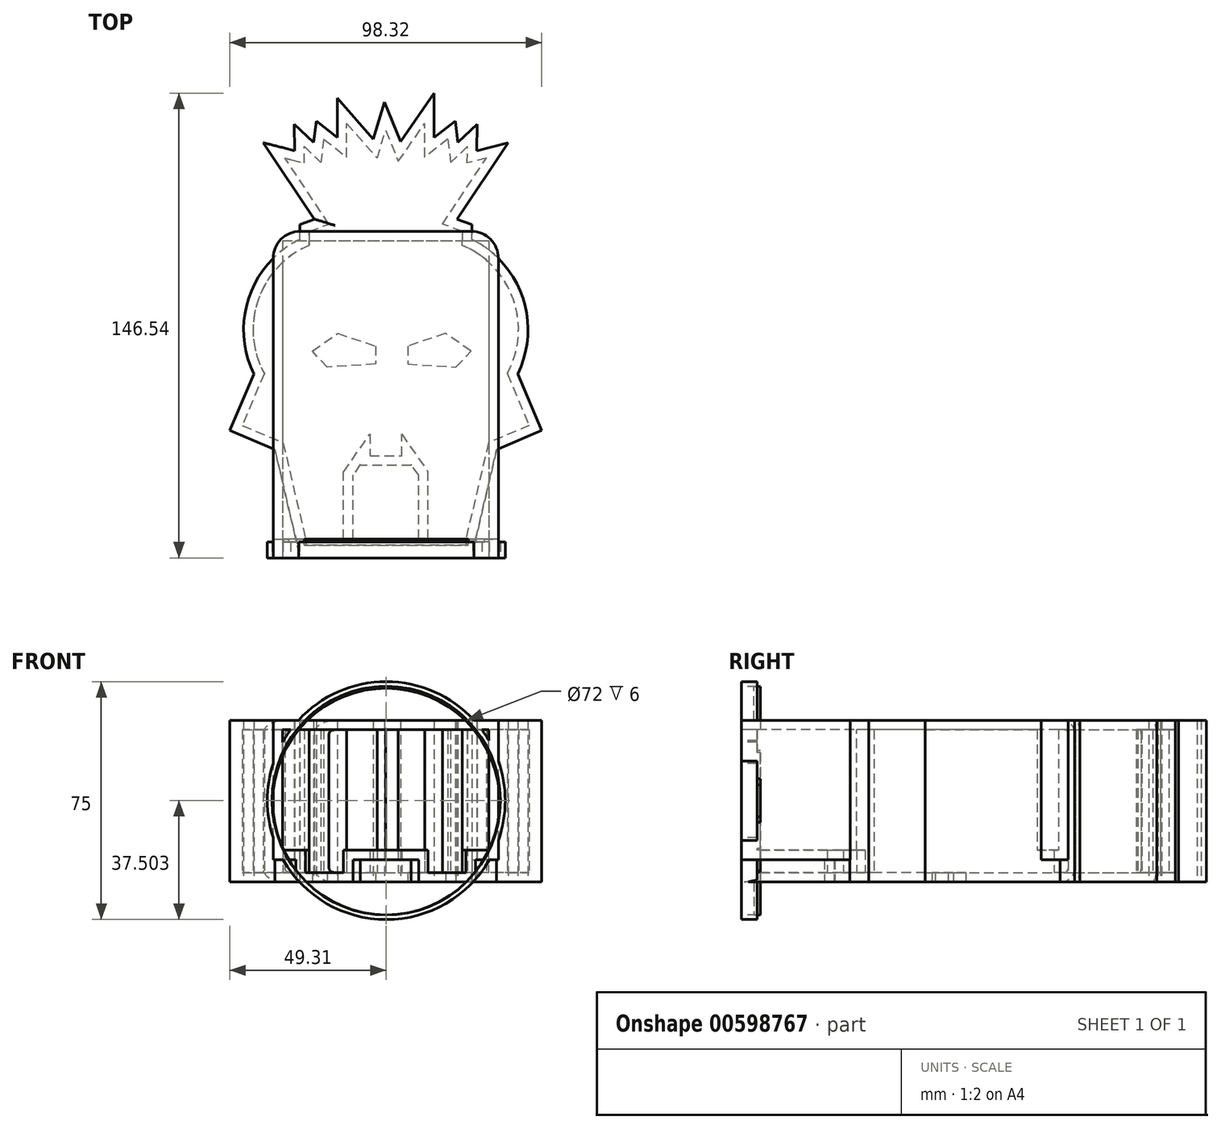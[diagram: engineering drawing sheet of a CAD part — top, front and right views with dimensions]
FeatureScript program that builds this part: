
annotation { "Feature Type Name" : "Feature", "Feature Type Description" : "" }
export const myFeature = defineFeature(function(context is Context, id is Id, definition is map)
    precondition{}
    {
        {
            var Q0;
            Q0=qCreatedBy(makeId("Top.planeOp"),FACE);
            var sketch = newSketch(context, id + "F0", { "sketchPlane" : qUnion([Q0])});
            skLineSegment(sketch, "E0", {"start": v(-38.3, -12.71) * mm, "end": v(-45.23, -29.07) * mm});
            skLineSegment(sketch, "E1", {"start": v(-45.23, -29.07) * mm, "end": v(-32.38, -34.51) * mm});
            skLineSegment(sketch, "E2", {"start": v(-32.38, -34.51) * mm, "end": v(-23.85, -70.83) * mm});
            skLineSegment(sketch, "E3", {"start": v(-23.85, -70.83) * mm, "end": v(-13.34, -70.83) * mm});
            skLineSegment(sketch, "E4", {"start": v(-13.34, -70.83) * mm, "end": v(-13.34, -43.75) * mm});
            skLineSegment(sketch, "E5", {"start": v(-13.34, -43.75) * mm, "end": v(-5, -31.79) * mm});
            skLineSegment(sketch, "E6", {"start": v(-5, -31.79) * mm, "end": v(-5, -38.64) * mm});
            skLineSegment(sketch, "E7", {"start": v(-5, -38.64) * mm, "end": v(0, -38.64) * mm});
            skLineSegment(sketch, "E8", {"start": v(-17.87, 34.44) * mm, "end": v(-31.74, 55.24) * mm});
            skLineSegment(sketch, "E9", {"start": v(-24.11, 32.15) * mm, "end": v(-17.87, 34.44) * mm});
            skLineSegment(sketch, "E10", {"start": v(-25.74, 58.87) * mm, "end": v(-20.48, 53.84) * mm});
            skLineSegment(sketch, "E11", {"start": v(-12.28, 55.5) * mm, "end": v(-12.28, 66.16) * mm});
            skLineSegment(sketch, "E12", {"start": v(-12.28, 66.16) * mm, "end": v(-2.75, 55.24) * mm});
            skLineSegment(sketch, "E13", {"start": v(-2.75, 55.24) * mm, "end": v(0, 64) * mm});
            skLineSegment(sketch, "E14", {"start": v(-19.56, 61.27) * mm, "end": v(-12.28, 55.5) * mm});
            skLineSegment(sketch, "E15", {"start": v(-19.56, 61.27) * mm, "end": v(-20.48, 53.84) * mm});
            skArc(sketch, "E16", {"start": v(-24.11, 27.73) * mm, "mid": v(-40.2, 10.66) * mm, "end": v(-38.3, -12.71) * mm});
            skLineSegment(sketch, "E17", {"start": v(-31.74, 55.24) * mm, "end": v(-25.67, 53.67) * mm});
            skLineSegment(sketch, "E18", {"start": v(-25.67, 53.67) * mm, "end": v(-25.74, 58.87) * mm});
            skLineSegment(sketch, "E19", {"start": v(0, 79.09) * mm, "end": v(0, -69.65) * mm, "construction": true});
            skLineSegment(sketch, "E20.MirrorCS", {"start": v(25.67, 53.67) * mm, "end": v(25.74, 58.87) * mm});
            skLineSegment(sketch, "E21.MirrorCS", {"start": v(19.56, 61.27) * mm, "end": v(20.48, 53.84) * mm});
            skLineSegment(sketch, "E22.MirrorCS", {"start": v(19.56, 61.27) * mm, "end": v(12.28, 55.5) * mm});
            skLineSegment(sketch, "E23.MirrorCS", {"start": v(12.28, 55.5) * mm, "end": v(12.28, 66.16) * mm});
            skLineSegment(sketch, "E24.MirrorCS", {"start": v(25.74, 58.87) * mm, "end": v(20.48, 53.84) * mm});
            skLineSegment(sketch, "E25.MirrorCS", {"start": v(31.74, 55.24) * mm, "end": v(25.67, 53.67) * mm});
            skLineSegment(sketch, "E26.MirrorCS", {"start": v(24.11, 32.15) * mm, "end": v(17.87, 34.44) * mm});
            skLineSegment(sketch, "E27.MirrorCS", {"start": v(23.85, -70.83) * mm, "end": v(13.34, -70.83) * mm});
            skLineSegment(sketch, "E28.MirrorCS", {"start": v(32.38, -34.51) * mm, "end": v(23.85, -70.83) * mm});
            skLineSegment(sketch, "E29.MirrorCS", {"start": v(17.87, 34.44) * mm, "end": v(31.74, 55.24) * mm});
            skLineSegment(sketch, "E30.MirrorCS", {"start": v(13.34, -70.83) * mm, "end": v(13.34, -43.75) * mm});
            skLineSegment(sketch, "E31.MirrorCS", {"start": v(45.23, -29.07) * mm, "end": v(32.38, -34.51) * mm});
            skLineSegment(sketch, "E32.MirrorCS", {"start": v(38.3, -12.71) * mm, "end": v(45.23, -29.07) * mm});
            skArc(sketch, "E33.MirrorCS", {"start": v(24.11, 27.73) * mm, "mid": v(40.2, 10.66) * mm, "end": v(38.3, -12.71) * mm});
            skLineSegment(sketch, "E34", {"start": v(0, 64) * mm, "end": v(3.95, 54.2) * mm});
            skLineSegment(sketch, "E35", {"start": v(3.95, 54.2) * mm, "end": v(12.28, 66.16) * mm});
            skLineSegment(sketch, "E36", {"start": v(0, -38.64) * mm, "end": v(5, -38.64) * mm});
            skLineSegment(sketch, "E37", {"start": v(5, -38.64) * mm, "end": v(5, -31.79) * mm});
            skLineSegment(sketch, "E38", {"start": v(5, -31.79) * mm, "end": v(13.34, -43.75) * mm});
            skLineSegment(sketch, "E39", {"start": v(-24.11, 32.15) * mm, "end": v(-24.11, 27.73) * mm});
            skLineSegment(sketch, "E40", {"start": v(24.11, 32.15) * mm, "end": v(24.11, 27.73) * mm});
            skSolve(sketch);
        }
        {
            var Q0;
            Q0=qSketchRegion(id+"F0",true);
            extrude(context, id + "F1", {"entities" : qUnion([Q0]), "depth" : 45 * mm, "offsetDistance" : 25 * mm});
        }
        {
            var Q0;
            Q0=qCreatedBy(makeId("Top.planeOp"),FACE);
            var sketch = newSketch(context, id + "F2", { "sketchPlane" : qUnion([Q0])});
            skLineSegment(sketch, "E41", {"start": v(-23.16, -5.6) * mm, "end": v(-18.41, -10.67) * mm});
            skLineSegment(sketch, "E42", {"start": v(-18.41, -10.67) * mm, "end": v(-3.2, -9.69) * mm});
            skLineSegment(sketch, "E43", {"start": v(-3.2, -9.69) * mm, "end": v(-3.2, -4.02) * mm});
            skLineSegment(sketch, "E44", {"start": v(-3.2, -4.02) * mm, "end": v(-15.14, 0) * mm});
            skLineSegment(sketch, "E45", {"start": v(-15.14, 0) * mm, "end": v(-23.16, -5.6) * mm});
            skLineSegment(sketch, "E46", {"start": v(-15.14, 0) * mm, "end": v(-10.75, -1.03) * mm});
            skFitSpline(sketch, "E47", {"points": [v(-10.75, -1.03) * mm, v(-10.75, 2.44) * mm, v(-12.29, 3.2) * mm, v(-11.11, 6.02) * mm], "startDerivative": vector(-4.83, 8.14) * mm, "endDerivative": vector(5.33, 8.63) * mm});
            skLineSegment(sketch, "E48", {"start": v(1.86, -15.53) * mm, "end": v(1.86, 7.72) * mm, "construction": true});
            skLineSegment(sketch, "E49.MirrorCS", {"start": v(6.93, -9.69) * mm, "end": v(6.93, -4.02) * mm});
            skLineSegment(sketch, "E50.MirrorCS", {"start": v(22.13, -10.67) * mm, "end": v(6.93, -9.69) * mm});
            skLineSegment(sketch, "E51.MirrorCS", {"start": v(6.93, -4.02) * mm, "end": v(18.86, 0) * mm});
            skLineSegment(sketch, "E52.MirrorCS", {"start": v(26.88, -5.6) * mm, "end": v(22.13, -10.67) * mm});
            skLineSegment(sketch, "E53.MirrorCS", {"start": v(18.86, 0) * mm, "end": v(26.88, -5.6) * mm});
            skLineSegment(sketch, "E54.MirrorCS", {"start": v(18.86, 0) * mm, "end": v(14.47, -1.03) * mm});
            skFitSpline(sketch, "E55.MirrorCS", {"points": [v(14.47, -1.03) * mm, v(14.47, 2.44) * mm, v(16, 3.2) * mm, v(14.84, 6.02) * mm], "startDerivative": vector(4.83, 8.14) * mm, "endDerivative": vector(-5.33, 8.63) * mm});
            skPoint(sketch, "E56", {"position": v(1.86, 13.91) * mm});
            skSolve(sketch);
        }
        {
            var Q0;
            Q0=makeQuery(id+"F1.opExtrude","CAP_EDGE",EDGE,{"disambiguationData":[OSD([sQuery(id+"F0.wireOp",EDGE,"QlBGKe7W-CjFm-zpKe-syDU-rIZYVbdessFk")])],"isStart":false});
            var Q1;
            Q1=makeQuery(id+"F1.opExtrude","CAP_EDGE",EDGE,{"disambiguationData":[OSD([sQuery(id+"F0.wireOp",EDGE,"E210.MirrorCS")])],"isStart":false});
            var Q2;
            Q2=makeQuery(id+"F1.opExtrude","CAP_EDGE",EDGE,{"disambiguationData":[OSD([sQuery(id+"F0.wireOp",EDGE,"E9")])],"isStart":false});
            var Q3;
            Q3=makeQuery(id+"F1.opExtrude","CAP_EDGE",EDGE,{"disambiguationData":[OSD([sQuery(id+"F0.wireOp",EDGE,"E26.MirrorCS")])],"isStart":false});
            fillet(context, id + "F3", {"entities" : qUnion([Q0, Q1, Q2, Q3]), "radius" : 1.02 * mm, "tangentPropagation" : true, "allowEdgeOverflow" : false});
        }
        {
            var Q0;
            Q0=makeQuery(id+"F3.opFillet","BLEND_EDGE",EDGE,{"blendedFrom":[makeQuery(id+"F1.opExtrude","CAP_EDGE",EDGE,{"disambiguationData":[OSD([sQuery(id+"F0.wireOp",EDGE,"E9")])],"isStart":false}),makeQuery(id+"F1.opExtrude","CAP_EDGE",EDGE,{"disambiguationData":[OSD([sQuery(id+"F0.wireOp",EDGE,"QlBGKe7W-CjFm-zpKe-syDU-rIZYVbdessFk")])],"isStart":false})],"blendedInto":[]});
            var Q1;
            Q1=makeQuery(id+"F3.opFillet","BLEND_EDGE",EDGE,{"blendedFrom":[makeQuery(id+"F1.opExtrude","CAP_EDGE",EDGE,{"disambiguationData":[OSD([sQuery(id+"F0.wireOp",EDGE,"E26.MirrorCS")])],"isStart":false}),makeQuery(id+"F1.opExtrude","CAP_EDGE",EDGE,{"disambiguationData":[OSD([sQuery(id+"F0.wireOp",EDGE,"E210.MirrorCS")])],"isStart":false})],"blendedInto":[]});
            var Q2;
            Q2=makeQuery(id+"F1.opExtrude","CAP_EDGE",EDGE,{"disambiguationData":[OSD([sQuery(id+"F0.wireOp",EDGE,"E8")])],"isStart":false});
            var Q3;
            Q3=makeQuery(id+"F1.opExtrude","CAP_EDGE",EDGE,{"disambiguationData":[OSD([sQuery(id+"F0.wireOp",EDGE,"E29.MirrorCS")])],"isStart":false});
            var Q4;
            Q4=makeQuery(id+"F1.opExtrude","CAP_EDGE",EDGE,{"disambiguationData":[OSD([sQuery(id+"F0.wireOp",EDGE,"E8")])],"isStart":true});
            var Q5;
            Q5=makeQuery(id+"F1.opExtrude","CAP_EDGE",EDGE,{"disambiguationData":[OSD([sQuery(id+"F0.wireOp",EDGE,"E29.MirrorCS")])],"isStart":true});
            var Q6;
            Q6=makeQuery(id+"F1.opExtrude","CAP_EDGE",EDGE,{"disambiguationData":[OSD([sQuery(id+"F0.wireOp",EDGE,"E26.MirrorCS")])],"isStart":true});
            var Q7;
            Q7=makeQuery(id+"F1.opExtrude","CAP_EDGE",EDGE,{"disambiguationData":[OSD([sQuery(id+"F0.wireOp",EDGE,"E210.MirrorCS")])],"isStart":true});
            var Q8;
            Q8=makeQuery(id+"F1.opExtrude","CAP_EDGE",EDGE,{"disambiguationData":[OSD([sQuery(id+"F0.wireOp",EDGE,"QlBGKe7W-CjFm-zpKe-syDU-rIZYVbdessFk")])],"isStart":true});
            var Q9;
            Q9=makeQuery(id+"F1.opExtrude","CAP_EDGE",EDGE,{"disambiguationData":[OSD([sQuery(id+"F0.wireOp",EDGE,"E9")])],"isStart":true});
            fillet(context, id + "F4", {"entities" : qUnion([Q0, Q1, Q2, Q3, Q4, Q5, Q6, Q7, Q8, Q9]), "radius" : 1.27 * mm, "tangentPropagation" : true, "allowEdgeOverflow" : false});
        }
        {
            var Q0;
            Q0=makeQuery(id+"F1.opExtrude","CAP_FACE",FACE,{"disambiguationData":[OSD([sQuery(id+"F0.wireOp",EDGE,"E0"),sQuery(id+"F0.wireOp",EDGE,"E1"),sQuery(id+"F0.wireOp",EDGE,"E2"),sQuery(id+"F0.wireOp",EDGE,"E3"),sQuery(id+"F0.wireOp",EDGE,"E4"),sQuery(id+"F0.wireOp",EDGE,"E5"),sQuery(id+"F0.wireOp",EDGE,"E6"),sQuery(id+"F0.wireOp",EDGE,"E7"),sQuery(id+"F0.wireOp",EDGE,"QlBGKe7W-CjFm-zpKe-syDU-rIZYVbdessFk"),sQuery(id+"F0.wireOp",EDGE,"E8"),sQuery(id+"F0.wireOp",EDGE,"E9"),sQuery(id+"F0.wireOp",EDGE,"E10"),sQuery(id+"F0.wireOp",EDGE,"E11"),sQuery(id+"F0.wireOp",EDGE,"YeJSSkTn-FtL6-i8Rl-ahXc-JzPqReOcuTEl"),sQuery(id+"F0.wireOp",EDGE,"0AvRNHQZ-9jO7-RX2F-YmTK-DABBuAo3s7oE"),sQuery(id+"F0.wireOp",EDGE,"xWFMa1az-Kvkm-zQS0-EvPk-zAxefn89ps1X"),sQuery(id+"F0.wireOp",EDGE,"PtLbIQZY-IS9e-ehaK-3uLq-SwewusbjE9fL"),sQuery(id+"F0.wireOp",EDGE,"E12"),sQuery(id+"F0.wireOp",EDGE,"E13"),sQuery(id+"F0.wireOp",EDGE,"E14"),sQuery(id+"F0.wireOp",EDGE,"E15"),sQuery(id+"F0.wireOp",EDGE,"E16"),sQuery(id+"F0.wireOp",EDGE,"E17"),sQuery(id+"F0.wireOp",EDGE,"E18"),sQuery(id+"F0.wireOp",EDGE,"E20.MirrorCS"),sQuery(id+"F0.wireOp",EDGE,"E21.MirrorCS"),sQuery(id+"F0.wireOp",EDGE,"E22.MirrorCS"),sQuery(id+"F0.wireOp",EDGE,"E23.MirrorCS"),sQuery(id+"F0.wireOp",EDGE,"E24.MirrorCS"),sQuery(id+"F0.wireOp",EDGE,"8db37806-3d3e-4eaf-9e43-167e2250198d6.MirrorCS"),sQuery(id+"F0.wireOp",EDGE,"8db37806-3d3e-4eaf-9e43-167e2250198d8.MirrorCS"),sQuery(id+"F0.wireOp",EDGE,"E210.MirrorCS"),sQuery(id+"F0.wireOp",EDGE,"E26.MirrorCS"),sQuery(id+"F0.wireOp",EDGE,"E27.MirrorCS"),sQuery(id+"F0.wireOp",EDGE,"E25.MirrorCS"),sQuery(id+"F0.wireOp",EDGE,"83e56f64-14f1-453a-9d83-025f2e8a94ae3.MirrorCS"),sQuery(id+"F0.wireOp",EDGE,"E31.MirrorCS"),sQuery(id+"F0.wireOp",EDGE,"E29.MirrorCS"),sQuery(id+"F0.wireOp",EDGE,"E30.MirrorCS"),sQuery(id+"F0.wireOp",EDGE,"E28.MirrorCS"),sQuery(id+"F0.wireOp",EDGE,"E32.MirrorCS"),sQuery(id+"F0.wireOp",EDGE,"E33.MirrorCS"),sQuery(id+"F0.wireOp",EDGE,"E34"),sQuery(id+"F0.wireOp",EDGE,"E35"),sQuery(id+"F0.wireOp",EDGE,"KlBAluSZ-iXYF-gunQ-GgUj-j9AXwpjWbuxS"),sQuery(id+"F0.wireOp",EDGE,"E36"),sQuery(id+"F0.wireOp",EDGE,"E37"),sQuery(id+"F0.wireOp",EDGE,"E38")])],"isStart":true});
            var sketch = newSketch(context, id + "F5", { "sketchPlane" : qUnion([Q0])});
            skLineSegment(sketch, "E57", {"start": v(15.92, -33.8) * mm, "end": v(-15.92, -33.8) * mm});
            skSolve(sketch);
        }
        {
            var Q0;
            Q0=qSketchRegion(id+"F5",true);
            var Q1;
            Q1=sQuery(id+"F5.wireOp",EDGE,"E57");
            extrude(context, id + "F6", {"entities" : qUnion([Q0]), "bodyType" : ToolBodyType.SURFACE, "operationType" : NewBodyOperationType.REMOVE, "surfaceEntities" : qUnion([Q1]), "oppositeDirection" : true, "depth" : 0.25 * mm});
        }
        {
            var Q0;
            Q0=makeQuery(id+"F1.opExtrude","SWEPT_FACE",FACE,{"disambiguationData":[OSD([sQuery(id+"F0.wireOp",EDGE,"E3")])]});
            var sketch = newSketch(context, id + "F7", { "sketchPlane" : qUnion([Q0])});
            skCircle(sketch, "E58", {"center": v(-13.34, 22.5) * mm, "radius": 37.5 * mm});
            skLineSegment(sketch, "E59", {"start": v(-13.34, 22.5) * mm, "end": v(13.87, 22.5) * mm});
            skSolve(sketch);
        }
        {
            var Q0;
            Q0=makeQuery(id+"F7.imprint","IMPRINT",FACE,{"disambiguationData":[TD([[makeQuery(id+"F7.imprint","IMPRINT",EDGE,{"derivedFrom":sQuery(id+"F7.wireOp",EDGE,"E58")}),1.0]])]});
            var sketch = newSketch(context, id + "F8", { "sketchPlane" : qUnion([Q0])});
            skLineSegment(sketch, "E60.bottom", {"start": v(-32.5, 45.03) * mm, "end": v(32.5, 45.03) * mm});
            skLineSegment(sketch, "E60.top", {"start": v(-32.5, 7.03) * mm, "end": v(32.5, 7.03) * mm});
            skLineSegment(sketch, "E60.left", {"start": v(-32.5, 45.03) * mm, "end": v(-32.5, 7.03) * mm});
            skLineSegment(sketch, "E60.right", {"start": v(32.5, 45.03) * mm, "end": v(32.5, 7.03) * mm});
            skSolve(sketch);
        }
        {
            var Q0;
            Q0 = qSketchRegion(id + "F8", true);
            extrude(context, id + "F9", {"entities" : qUnion([Q0]), "operationType" : NewBodyOperationType.ADD, "oppositeDirection" : true, "depth" : 100 * mm, "offsetDistance" : 25 * mm});
        }
        {
            var Q0;
            Q0=makeQuery(id+"F9.boolean.opBoolean","MERGE",FACE,{"derivedFrom":[makeQuery(id+"F1.opExtrude","SWEPT_FACE",FACE,{"disambiguationData":[OSD([sQuery(id+"F0.wireOp",EDGE,"E3")])]}),makeQuery(id+"F1.opExtrude","SWEPT_FACE",FACE,{"disambiguationData":[OSD([sQuery(id+"F0.wireOp",EDGE,"E27.MirrorCS")])]}),makeQuery(id+"F9.opExtrude","CAP_FACE",FACE,{"disambiguationData":[OSD([sQuery(id+"F8.wireOp",EDGE,"E60.bottom"),sQuery(id+"F8.wireOp",EDGE,"E60.top"),sQuery(id+"F8.wireOp",EDGE,"E60.left"),sQuery(id+"F8.wireOp",EDGE,"E60.right")])],"isStart":true})]});
            shell(context, id + "F10", {"entities" : qUnion([Q0]), "thickness" : 3 * mm, "oppositeDirection" : true});
        }
        {
            var Q0;
            Q0=makeQuery(id+"F9.opExtrude","CAP_EDGE",EDGE,{"disambiguationData":[OSD([sQuery(id+"F8.wireOp",EDGE,"E60.left")])],"isStart":false});
            var Q1;
            Q1=makeQuery(id+"F9.opExtrude","CAP_EDGE",EDGE,{"disambiguationData":[OSD([sQuery(id+"F8.wireOp",EDGE,"E60.right")])],"isStart":false});
            fillet(context, id + "F11", {"entities" : qUnion([Q0, Q1]), "radius" : 8.5 * mm, "tangentPropagation" : true, "allowEdgeOverflow" : false});
        }
        {
            var Q0;
            Q0 = qSketchRegion(id + "F2", true);
            extrude(context, id + "F12", {"entities" : qUnion([Q0]), "operationType" : NewBodyOperationType.REMOVE, "endBound" : BoundingType.SYMMETRIC, "depth" : 10 * mm, "offsetDistance" : 25 * mm});
        }
        {
            var Q0;
            Q0=makeQuery(id+"F7.imprint","IMPRINT",FACE,{"disambiguationData":[TD([[makeQuery(id+"F7.imprint","IMPRINT",EDGE,{"derivedFrom":sQuery(id+"F7.wireOp",EDGE,"E58")}),1.0]])]});
            var sketch = newSketch(context, id + "F13", { "sketchPlane" : qUnion([Q0])});
            skCircle(sketch, "E61", {"center": v(0.15, 22.7) * mm, "radius": 37.5 * mm});
            skSolve(sketch);
        }
        {
            var Q0;
            Q0 = qSketchRegion(id + "F13", true);
            extrude(context, id + "F14", {"entities" : qUnion([Q0]), "operationType" : NewBodyOperationType.ADD, "oppositeDirection" : true, "depth" : 5 * mm, "offsetDistance" : 25 * mm});
        }
        {
            var Q0;
            Q0=makeQuery(id+"F14.boolean.opBoolean","MERGE",FACE,{"derivedFrom":[makeQuery(id+"F9.boolean.opBoolean","MERGE",FACE,{"derivedFrom":[makeQuery(id+"F1.opExtrude","SWEPT_FACE",FACE,{"disambiguationData":[OSD([sQuery(id+"F0.wireOp",EDGE,"E3")])]}),makeQuery(id+"F1.opExtrude","SWEPT_FACE",FACE,{"disambiguationData":[OSD([sQuery(id+"F0.wireOp",EDGE,"E27.MirrorCS")])]}),makeQuery(id+"F9.opExtrude","CAP_FACE",FACE,{"disambiguationData":[OSD([sQuery(id+"F8.wireOp",EDGE,"E60.bottom"),sQuery(id+"F8.wireOp",EDGE,"E60.top"),sQuery(id+"F8.wireOp",EDGE,"E60.left"),sQuery(id+"F8.wireOp",EDGE,"E60.right")])],"isStart":true})]}),makeQuery(id+"F14.opExtrude","CAP_FACE",FACE,{"disambiguationData":[OSD([sQuery(id+"F13.wireOp",EDGE,"E61")])],"isStart":true})]});
            var sketch = newSketch(context, id + "F15", { "sketchPlane" : qUnion([Q0])});
            skCircle(sketch, "E62", {"center": v(0.15, 22.7) * mm, "radius": 36 * mm});
            skSolve(sketch);
        }
        {
            var Q0;
            Q0 = qSketchRegion(id + "F15", true);
            extrude(context, id + "F16", {"entities" : qUnion([Q0]), "operationType" : NewBodyOperationType.REMOVE, "oppositeDirection" : true, "depth" : 6 * mm, "offsetDistance" : 25 * mm});
        }
        {
            var Q0;
            {var subQ47=sQuery(id+"F0.wireOp",EDGE,"E2");var subQ52=makeQuery(id+"F1.opExtrude","SWEPT_FACE",FACE,{"disambiguationData":[OSD([subQ47])]});var subQ53=sQuery(id+"F15.wireOp",EDGE,"E62");Q0=makeQuery(id+"F16.boolean.opBoolean","COPY",FACE,{"disambiguationData":[TD([subQ52])],"derivedFrom":makeQuery(id+"F16.opExtrude","CAP_FACE",FACE,{"disambiguationData":[OSD([subQ53])],"isStart":false})});}
            var sketch = newSketch(context, id + "F17", { "sketchPlane" : qUnion([Q0])});
            skLineSegment(sketch, "E63", {"start": v(-25.07, -3) * mm, "end": v(25.37, -3) * mm});
            skArc(sketch, "E64", {"start": v(-25.07, -3) * mm, "mid": v(0.15, -13.41) * mm, "end": v(25.37, -3) * mm});
            skLineSegment(sketch, "E65", {"start": v(-25.67, 48.03) * mm, "end": v(26, 48.03) * mm});
            skArc(sketch, "E66", {"start": v(26, 48.03) * mm, "mid": v(0.17, 58.66) * mm, "end": v(-25.67, 48.03) * mm});
            skSolve(sketch);
        }
        {
            var Q0;
            Q0 = qSketchRegion(id + "F17", true);
            extrude(context, id + "F18", {"entities" : qUnion([Q0]), "depth" : 2 * mm, "offsetDistance" : 25 * mm});
        }
    });
